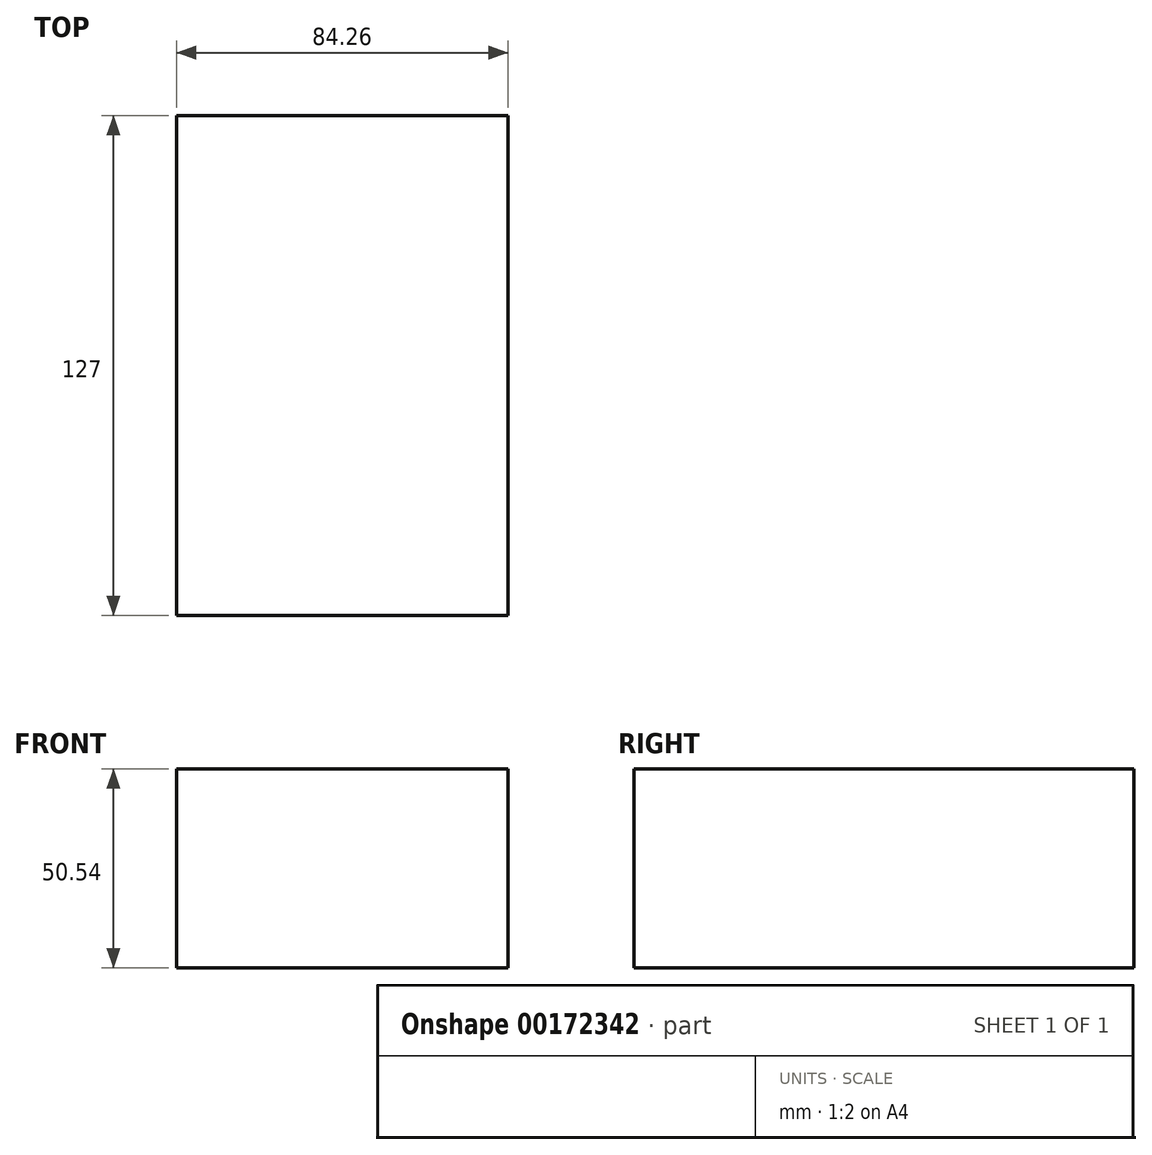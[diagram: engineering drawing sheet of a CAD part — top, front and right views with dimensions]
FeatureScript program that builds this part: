
annotation { "Feature Type Name" : "Feature", "Feature Type Description" : "" }
export const myFeature = defineFeature(function(context is Context, id is Id, definition is map)
    precondition{}
    {
        {
            var Q0;
            Q0=qCreatedBy(makeId("Front.planeOp"),FACE);
            var sketch = newSketch(context, id + "F0", { "sketchPlane" : qUnion([Q0])});
            skLineSegment(sketch, "E0.bottom", {"start": v(-53.77, 50.54) * mm, "end": v(30.5, 50.54) * mm});
            skLineSegment(sketch, "E0.top", {"start": v(-53.77, 0) * mm, "end": v(30.5, 0) * mm});
            skLineSegment(sketch, "E0.left", {"start": v(-53.77, 50.54) * mm, "end": v(-53.77, 0) * mm});
            skLineSegment(sketch, "E0.right", {"start": v(30.5, 50.54) * mm, "end": v(30.5, 0) * mm});
            skSolve(sketch);
        }
        {
            var Q0;
            Q0=makeQuery(id+"F0.imprint","IMPRINT",FACE,{"disambiguationData":[TD([[makeQuery(id+"F0.imprint","IMPRINT",EDGE,{"derivedFrom":sQuery(id+"F0.wireOp",EDGE,"E0.bottom")}),-1.0]])]});
            extrude(context, id + "F1", {"entities" : qUnion([Q0]), "depth" : 127 * mm});
        }
    });
